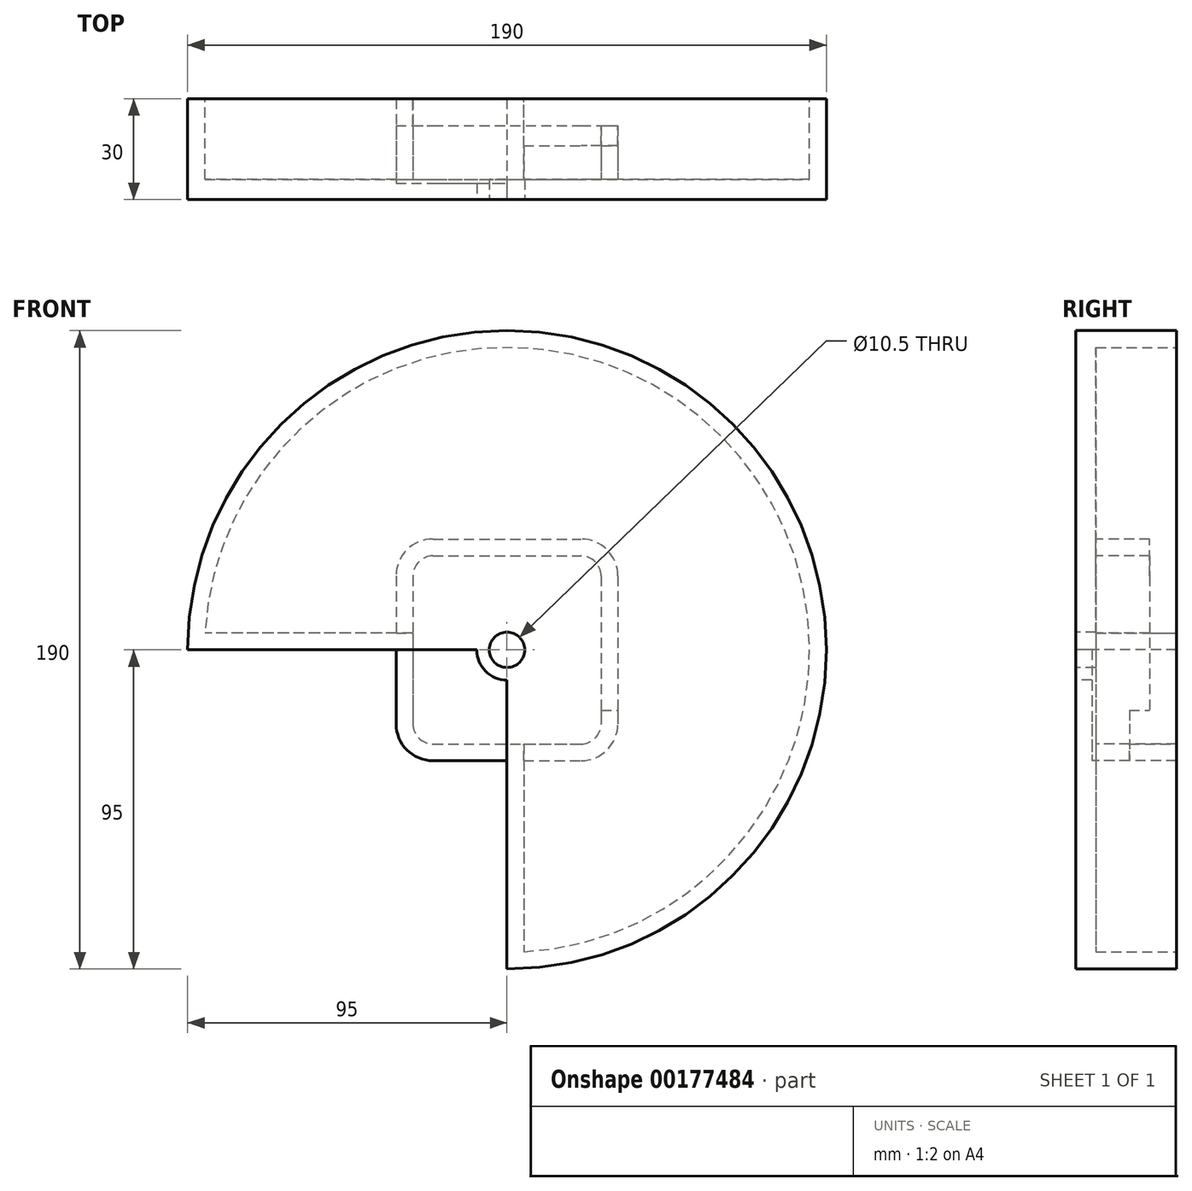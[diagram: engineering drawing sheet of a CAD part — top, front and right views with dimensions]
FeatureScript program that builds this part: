
annotation { "Feature Type Name" : "Feature", "Feature Type Description" : "" }
export const myFeature = defineFeature(function(context is Context, id is Id, definition is map)
    precondition{}
    {
        {
            var Q0;
            Q0=qCreatedBy(makeId("Front.planeOp"),FACE);
            var sketch = newSketch(context, id + "F0", { "sketchPlane" : qUnion([Q0])});
            skCircle(sketch, "E0", {"center": v(0, 0) * mm, "radius": 95 * mm});
            skSolve(sketch);
        }
        {
            var Q0;
            Q0 = qSketchRegion(id + "F0", true);
            extrude(context, id + "F1", {"entities" : qUnion([Q0]), "depth" : 30 * mm});
        }
        {
            var Q0;
            Q0=makeQuery(id+"F1.opExtrude","CAP_FACE",FACE,{"disambiguationData":[OSD([sQuery(id+"F0.wireOp",EDGE,"E0")])],"isStart":false});
            var sketch = newSketch(context, id + "F2", { "sketchPlane" : qUnion([Q0])});
            skLineSegment(sketch, "E1.bottom", {"start": v(-95, 0) * mm, "end": v(0, 0) * mm});
            skLineSegment(sketch, "E1.top", {"start": v(-95, -95) * mm, "end": v(0, -95) * mm});
            skLineSegment(sketch, "E1.left", {"start": v(-95, 0) * mm, "end": v(-95, -95) * mm});
            skLineSegment(sketch, "E1.right", {"start": v(0, 0) * mm, "end": v(0, -95) * mm});
            skSolve(sketch);
        }
        {
            var Q0;
            Q0 = qSketchRegion(id + "F2", true);
            extrude(context, id + "F3", {"entities" : qUnion([Q0]), "operationType" : NewBodyOperationType.REMOVE, "oppositeDirection" : true, "depth" : 40 * mm});
        }
        {
            var Q0;
            Q0=makeQuery(id+"F1.opExtrude","CAP_FACE",FACE,{"disambiguationData":[OSD([sQuery(id+"F0.wireOp",EDGE,"E0")])],"isStart":false});
            var sketch = newSketch(context, id + "F4", { "sketchPlane" : qUnion([Q0])});
            skCircle(sketch, "E2", {"center": v(0, 0) * mm, "radius": 9 * mm});
            skSolve(sketch);
        }
        {
            var Q0;
            Q0 = qSketchRegion(id + "F4", true);
            extrude(context, id + "F5", {"entities" : qUnion([Q0]), "operationType" : NewBodyOperationType.ADD, "oppositeDirection" : true, "depth" : 30 * mm});
        }
        {
            var Q0;
            Q0=makeQuery(id+"F5.boolean.opBoolean","MERGE",FACE,{"derivedFrom":[makeQuery(id+"F1.opExtrude","CAP_FACE",FACE,{"disambiguationData":[OSD([sQuery(id+"F0.wireOp",EDGE,"E0")])],"isStart":false}),makeQuery(id+"F5.opExtrude","CAP_FACE",FACE,{"disambiguationData":[OSD([sQuery(id+"F4.wireOp",EDGE,"E2")])],"isStart":true})]});
            var sketch = newSketch(context, id + "F6", { "sketchPlane" : qUnion([Q0])});
            skCircle(sketch, "E3", {"center": v(0, 0) * mm, "radius": 5.25 * mm});
            skSolve(sketch);
        }
        {
            var Q0;
            Q0 = qSketchRegion(id + "F6", true);
            extrude(context, id + "F7", {"entities" : qUnion([Q0]), "operationType" : NewBodyOperationType.REMOVE, "oppositeDirection" : true, "depth" : 40 * mm});
        }
        {
            var Q0;
            Q0=makeQuery(id+"F5.boolean.opBoolean","MERGE",FACE,{"derivedFrom":[makeQuery(id+"F1.opExtrude","CAP_FACE",FACE,{"disambiguationData":[OSD([sQuery(id+"F0.wireOp",EDGE,"E0")])],"isStart":true}),makeQuery(id+"F5.opExtrude","CAP_FACE",FACE,{"disambiguationData":[OSD([sQuery(id+"F4.wireOp",EDGE,"E2")])],"isStart":false})]});
            var sketch = newSketch(context, id + "F8", { "sketchPlane" : qUnion([Q0])});
            skCircle(sketch, "E4", {"center": v(0, 0) * mm, "radius": 90 * mm});
            skLineSegment(sketch, "E5.bottom", {"start": v(0, -95) * mm, "end": v(95, -95) * mm});
            skLineSegment(sketch, "E5.top", {"start": v(0, 0) * mm, "end": v(95, 0) * mm});
            skLineSegment(sketch, "E5.left", {"start": v(0, -95) * mm, "end": v(0, 0) * mm});
            skLineSegment(sketch, "E5.right", {"start": v(95, -95) * mm, "end": v(95, 0) * mm});
            skLineSegment(sketch, "E6.0", {"start": v(-5, 5) * mm, "end": v(95, 5) * mm});
            skLineSegment(sketch, "E6.1", {"start": v(-5, -95) * mm, "end": v(-5, 5) * mm});
            skSolve(sketch);
        }
        {
            var Q0;
            {var subQ5=makeQuery(id+"F5.opExtrude","CAP_EDGE",EDGE,{"disambiguationData":[OSD([sQuery(id+"F4.wireOp",EDGE,"E2")])],"isStart":false});Q0=makeQuery(id+"F8.imprint","IMPRINT",FACE,{"disambiguationData":[TD([[makeQuery(id+"F8.imprint","IMPRINT",EDGE,{"derivedFrom":subQ5}),1.0]])]});}
            var Q1;
            {var subQ0=sQuery(id+"F8.wireOp",EDGE,"E5.left");var subQ1=sQuery(id+"F8.wireOp",EDGE,"E5.top");var subQ2=makeQuery(id+"F8.imprint","INTERSECT",VERTEX,{"derivedFrom":[subQ1,subQ0]});Q1=makeQuery(id+"F8.imprint","IMPRINT",FACE,{"disambiguationData":[TD([[makeQuery(id+"F8.imprint","IMPRINT",EDGE,{"disambiguationData":[TD([[subQ2,-1.0]])],"derivedFrom":subQ1}),-1.0]])]});}
            var Q2;
            {var subQ0=sQuery(id+"F8.wireOp",EDGE,"E6.1");var subQ1=sQuery(id+"F8.wireOp",EDGE,"E6.0");var subQ2=makeQuery(id+"F8.imprint","INTERSECT",VERTEX,{"derivedFrom":[subQ1,subQ0]});Q2=makeQuery(id+"F8.imprint","IMPRINT",FACE,{"disambiguationData":[TD([[makeQuery(id+"F8.imprint","IMPRINT",EDGE,{"disambiguationData":[TD([[subQ2,-1.0]])],"derivedFrom":subQ1}),-1.0]])]});}
            var Q3;
            {var subQ0=sQuery(id+"F8.wireOp",EDGE,"E6.0");var subQ1=makeQuery(id+"F7.boolean.opBoolean","INTERSECT",EDGE,{"derivedFrom":[makeQuery(id+"F5.boolean.opBoolean","MERGE",FACE,{"derivedFrom":[makeQuery(id+"F1.opExtrude","CAP_FACE",FACE,{"disambiguationData":[OSD([sQuery(id+"F0.wireOp",EDGE,"E0")])],"isStart":true}),makeQuery(id+"F5.opExtrude","CAP_FACE",FACE,{"disambiguationData":[OSD([sQuery(id+"F4.wireOp",EDGE,"E2")])],"isStart":false})]}),makeQuery(id+"F7.opExtrude","SWEPT_FACE",FACE,{"disambiguationData":[OSD([sQuery(id+"F6.wireOp",EDGE,"E3")])]})]});var subQ2=makeQuery(id+"F8.imprint","INTERSECT",VERTEX,{"disambiguationData":[OD(0.0)],"derivedFrom":[subQ1,subQ0]});Q3=makeQuery(id+"F8.imprint","IMPRINT",FACE,{"disambiguationData":[TD([[makeQuery(id+"F8.imprint","IMPRINT",EDGE,{"disambiguationData":[TD([[subQ2,-1.0]])],"derivedFrom":subQ0}),1.0]])]});}
            var Q4;
            {var subQ0=sQuery(id+"F8.wireOp",EDGE,"E6.1");var subQ1=makeQuery(id+"F7.boolean.opBoolean","INTERSECT",EDGE,{"derivedFrom":[makeQuery(id+"F5.boolean.opBoolean","MERGE",FACE,{"derivedFrom":[makeQuery(id+"F1.opExtrude","CAP_FACE",FACE,{"disambiguationData":[OSD([sQuery(id+"F0.wireOp",EDGE,"E0")])],"isStart":true}),makeQuery(id+"F5.opExtrude","CAP_FACE",FACE,{"disambiguationData":[OSD([sQuery(id+"F4.wireOp",EDGE,"E2")])],"isStart":false})]}),makeQuery(id+"F7.opExtrude","SWEPT_FACE",FACE,{"disambiguationData":[OSD([sQuery(id+"F6.wireOp",EDGE,"E3")])]})]});var subQ2=makeQuery(id+"F8.imprint","INTERSECT",VERTEX,{"disambiguationData":[OD(0.0)],"derivedFrom":[subQ1,subQ0]});Q4=makeQuery(id+"F8.imprint","IMPRINT",FACE,{"disambiguationData":[TD([[makeQuery(id+"F8.imprint","IMPRINT",EDGE,{"disambiguationData":[TD([[subQ2,-1.0]])],"derivedFrom":subQ0}),1.0]])]});}
            var Q5;
            {var subQ1=sQuery(id+"F4.wireOp",EDGE,"E2");var subQ2=makeQuery(id+"F5.opExtrude","CAP_EDGE",EDGE,{"disambiguationData":[OSD([subQ1])],"isStart":false});Q5=makeQuery(id+"F8.imprint","IMPRINT",FACE,{"disambiguationData":[TD([[makeQuery(id+"F8.imprint","IMPRINT",EDGE,{"derivedFrom":subQ2}),-1.0]])]});}
            var Q6;
            {var subQ0=sQuery(id+"F8.wireOp",EDGE,"E6.0");var subQ1=sQuery(id+"F8.wireOp",EDGE,"E4");var subQ2=makeQuery(id+"F8.imprint","INTERSECT",VERTEX,{"derivedFrom":[subQ1,subQ0]});Q6=makeQuery(id+"F8.imprint","IMPRINT",FACE,{"disambiguationData":[TD([[makeQuery(id+"F8.imprint","IMPRINT",EDGE,{"disambiguationData":[TD([[subQ2,1.0]])],"derivedFrom":subQ1}),1.0]])]});}
            var Q7;
            {var subQ0=sQuery(id+"F8.wireOp",EDGE,"E6.1");var subQ1=sQuery(id+"F8.wireOp",EDGE,"E4");var subQ2=makeQuery(id+"F8.imprint","INTERSECT",VERTEX,{"derivedFrom":[subQ1,subQ0]});Q7=makeQuery(id+"F8.imprint","IMPRINT",FACE,{"disambiguationData":[TD([[makeQuery(id+"F8.imprint","IMPRINT",EDGE,{"disambiguationData":[TD([[subQ2,-1.0]])],"derivedFrom":subQ1}),1.0]])]});}
            var Q8;
            {var subQ7=sQuery(id+"F8.wireOp",EDGE,"E5.left");var subQ8=sQuery(id+"F8.wireOp",EDGE,"E5.top");var subQ9=makeQuery(id+"F8.imprint","INTERSECT",VERTEX,{"derivedFrom":[subQ8,subQ7]});Q8=makeQuery(id+"F8.imprint","IMPRINT",FACE,{"disambiguationData":[TD([[makeQuery(id+"F8.imprint","IMPRINT",EDGE,{"disambiguationData":[TD([[subQ9,-1.0]])],"derivedFrom":subQ8}),1.0]])]});}
            var Q9;
            {var subQ1=sQuery(id+"F8.wireOp",EDGE,"E4");var subQ5=sQuery(id+"F8.wireOp",EDGE,"E6.0");var subQ6=makeQuery(id+"F8.imprint","INTERSECT",VERTEX,{"derivedFrom":[subQ1,subQ5]});Q9=makeQuery(id+"F8.imprint","IMPRINT",FACE,{"disambiguationData":[TD([[makeQuery(id+"F8.imprint","IMPRINT",EDGE,{"disambiguationData":[TD([[subQ6,-1.0]])],"derivedFrom":subQ1}),1.0]])]});}
            extrude(context, id + "F9", {"entities" : qUnion([Q0, Q1, Q2, Q3, Q4, Q5, Q6, Q7, Q8, Q9]), "operationType" : NewBodyOperationType.REMOVE, "oppositeDirection" : true, "depth" : 24 * mm});
        }
        {
            var Q0;
            Q0=makeQuery(id+"F9.boolean.opBoolean","COPY",FACE,{"derivedFrom":makeQuery(id+"F9.opExtrude","CAP_FACE",FACE,{"disambiguationData":[OSD([sQuery(id+"F8.wireOp",EDGE,"E4")])],"isStart":false})});
            var sketch = newSketch(context, id + "F10", { "sketchPlane" : qUnion([Q0])});
            skLineSegment(sketch, "E7.bottom", {"start": v(28, 28) * mm, "end": v(-28, 28) * mm});
            skLineSegment(sketch, "E7.top", {"start": v(28, -28) * mm, "end": v(-28, -28) * mm});
            skLineSegment(sketch, "E7.left", {"start": v(28, 28) * mm, "end": v(28, -28) * mm});
            skLineSegment(sketch, "E7.right", {"start": v(-28, 28) * mm, "end": v(-28, -28) * mm});
            skPoint(sketch, "E7.middle", {"position": v(0, 0) * mm});
            skLineSegment(sketch, "E8.0", {"start": v(33, 33) * mm, "end": v(-33, 33) * mm});
            skLineSegment(sketch, "E8.1", {"start": v(33, 33) * mm, "end": v(33, -33) * mm});
            skLineSegment(sketch, "E8.2", {"start": v(33, -33) * mm, "end": v(-33, -33) * mm});
            skLineSegment(sketch, "E8.3", {"start": v(-33, 33) * mm, "end": v(-33, -33) * mm});
            skLineSegment(sketch, "E9.bottom", {"start": v(33, 0) * mm, "end": v(90, 0) * mm});
            skLineSegment(sketch, "E9.top", {"start": v(33, 5) * mm, "end": v(90, 5) * mm});
            skLineSegment(sketch, "E9.left", {"start": v(33, 0) * mm, "end": v(33, 5) * mm});
            skLineSegment(sketch, "E9.right", {"start": v(90, 0) * mm, "end": v(90, 5) * mm});
            skLineSegment(sketch, "E10.bottom", {"start": v(0, -33) * mm, "end": v(-5, -33) * mm});
            skLineSegment(sketch, "E10.top", {"start": v(0, -90) * mm, "end": v(-5, -90) * mm});
            skLineSegment(sketch, "E10.left", {"start": v(0, -33) * mm, "end": v(0, -90) * mm});
            skLineSegment(sketch, "E10.right", {"start": v(-5, -33) * mm, "end": v(-5, -90) * mm});
            skSolve(sketch);
        }
        {
            var Q0;
            Q0 = qSketchRegion(id + "F10", true);
            extrude(context, id + "F11", {"entities" : qUnion([Q0]), "operationType" : NewBodyOperationType.ADD, "depth" : 24 * mm});
        }
        {
            var Q0;
            Q0=makeQuery(id+"F11.opExtrude","CAP_FACE",FACE,{"disambiguationData":[OSD([sQuery(id+"F10.wireOp",EDGE,"E7.bottom"),sQuery(id+"F10.wireOp",EDGE,"E7.top"),sQuery(id+"F10.wireOp",EDGE,"E7.left"),sQuery(id+"F10.wireOp",EDGE,"E7.right"),sQuery(id+"F10.wireOp",EDGE,"E8.0"),sQuery(id+"F10.wireOp",EDGE,"E8.1"),sQuery(id+"F10.wireOp",EDGE,"E8.2"),sQuery(id+"F10.wireOp",EDGE,"E8.3"),sQuery(id+"F10.wireOp",EDGE,"E9.bottom"),sQuery(id+"F10.wireOp",EDGE,"E9.top"),sQuery(id+"F10.wireOp",EDGE,"E9.right"),sQuery(id+"F10.wireOp",EDGE,"E10.top"),sQuery(id+"F10.wireOp",EDGE,"E10.left"),sQuery(id+"F10.wireOp",EDGE,"E10.right")])],"isStart":true});
            var sketch = newSketch(context, id + "F12", { "sketchPlane" : qUnion([Q0])});
            skLineSegment(sketch, "E11.0", {"start": v(-28, -28) * mm, "end": v(0, -28) * mm});
            skLineSegment(sketch, "E12.0", {"start": v(-28, 0) * mm, "end": v(-28, -28) * mm});
            skLineSegment(sketch, "E13.0", {"start": v(0, -9) * mm, "end": v(0, -28) * mm});
            skArc(sketch, "E14.0", {"start": v(-9, 0) * mm, "mid": v(-6.36, -6.36) * mm, "end": v(0, -9) * mm});
            skLineSegment(sketch, "E15.0", {"start": v(-28, 0) * mm, "end": v(-9, 0) * mm});
            skLineSegment(sketch, "E16.0", {"start": v(0, -28) * mm, "end": v(0, -33) * mm});
            skLineSegment(sketch, "E17.0", {"start": v(-33, -33) * mm, "end": v(0, -33) * mm});
            skLineSegment(sketch, "E18.0", {"start": v(-33, 0) * mm, "end": v(-33, -33) * mm});
            skLineSegment(sketch, "E19.0", {"start": v(-33, 0) * mm, "end": v(-28, 0) * mm});
            skSolve(sketch);
        }
        {
            var Q0;
            Q0 = qSketchRegion(id + "F12", true);
            extrude(context, id + "F13", {"entities" : qUnion([Q0]), "operationType" : NewBodyOperationType.ADD, "depth" : 1.2 * mm});
        }
        {
            var Q0;
            Q0=makeQuery(id+"F11.boolean.opBoolean","MERGE",FACE,{"derivedFrom":[makeQuery(id+"F5.boolean.opBoolean","MERGE",FACE,{"derivedFrom":[makeQuery(id+"F1.opExtrude","CAP_FACE",FACE,{"disambiguationData":[OSD([sQuery(id+"F0.wireOp",EDGE,"E0")])],"isStart":true}),makeQuery(id+"F5.opExtrude","CAP_FACE",FACE,{"disambiguationData":[OSD([sQuery(id+"F4.wireOp",EDGE,"E2")])],"isStart":false})]}),makeQuery(id+"F11.opExtrude","CAP_FACE",FACE,{"disambiguationData":[OSD([sQuery(id+"F10.wireOp",EDGE,"E7.bottom"),sQuery(id+"F10.wireOp",EDGE,"E7.top"),sQuery(id+"F10.wireOp",EDGE,"E7.left"),sQuery(id+"F10.wireOp",EDGE,"E7.right"),sQuery(id+"F10.wireOp",EDGE,"E8.0"),sQuery(id+"F10.wireOp",EDGE,"E8.1"),sQuery(id+"F10.wireOp",EDGE,"E8.2"),sQuery(id+"F10.wireOp",EDGE,"E8.3"),sQuery(id+"F10.wireOp",EDGE,"E9.bottom"),sQuery(id+"F10.wireOp",EDGE,"E9.top"),sQuery(id+"F10.wireOp",EDGE,"E9.right"),sQuery(id+"F10.wireOp",EDGE,"E10.top"),sQuery(id+"F10.wireOp",EDGE,"E10.left"),sQuery(id+"F10.wireOp",EDGE,"E10.right")])],"isStart":false})]});
            var sketch = newSketch(context, id + "F14", { "sketchPlane" : qUnion([Q0])});
            skLineSegment(sketch, "E20.bottom", {"start": v(-33, 33) * mm, "end": v(33, 33) * mm});
            skLineSegment(sketch, "E20.top", {"start": v(-33, -33) * mm, "end": v(33, -33) * mm});
            skLineSegment(sketch, "E20.left", {"start": v(-33, 33) * mm, "end": v(-33, -33) * mm});
            skLineSegment(sketch, "E20.right", {"start": v(33, 33) * mm, "end": v(33, -33) * mm});
            skLineSegment(sketch, "E21.bottom", {"start": v(33, 5) * mm, "end": v(28, 5) * mm});
            skLineSegment(sketch, "E21.top", {"start": v(33, -28) * mm, "end": v(28, -28) * mm});
            skLineSegment(sketch, "E21.left", {"start": v(33, 5) * mm, "end": v(33, -28) * mm});
            skLineSegment(sketch, "E21.right", {"start": v(28, 5) * mm, "end": v(28, -28) * mm});
            skLineSegment(sketch, "E22.bottom", {"start": v(-5, -33) * mm, "end": v(33, -33) * mm});
            skLineSegment(sketch, "E22.top", {"start": v(-5, -28) * mm, "end": v(33, -28) * mm});
            skLineSegment(sketch, "E22.left", {"start": v(-5, -33) * mm, "end": v(-5, -28) * mm});
            skLineSegment(sketch, "E22.right", {"start": v(33, -33) * mm, "end": v(33, -28) * mm});
            skSolve(sketch);
        }
        {
            var Q0;
            Q0=makeQuery(id+"F14.imprint","IMPRINT",FACE,{"disambiguationData":[TD([[makeQuery(id+"F14.imprint","IMPRINT",EDGE,{"derivedFrom":sQuery(id+"F14.wireOp",EDGE,"E20.bottom")}),1.0]])]});
            extrude(context, id + "F15", {"entities" : qUnion([Q0]), "operationType" : NewBodyOperationType.REMOVE, "oppositeDirection" : true, "depth" : 8 * mm});
        }
        {
            var Q0;
            Q0=makeQuery(id+"F11.opExtrude","SWEPT_EDGE",EDGE,{"disambiguationData":[OSD([sQuery(id+"F10.wireOp",EDGE,"E7.top"),sQuery(id+"F10.wireOp",EDGE,"E7.left")])]});
            var Q1;
            Q1=makeQuery(id+"F11.opExtrude","SWEPT_EDGE",EDGE,{"disambiguationData":[OSD([sQuery(id+"F10.wireOp",EDGE,"E7.top"),sQuery(id+"F10.wireOp",EDGE,"E7.right")])]});
            var Q2;
            Q2=makeQuery(id+"F11.opExtrude","SWEPT_EDGE",EDGE,{"disambiguationData":[OSD([sQuery(id+"F10.wireOp",EDGE,"E7.bottom"),sQuery(id+"F10.wireOp",EDGE,"E7.right")])]});
            var Q3;
            Q3=makeQuery(id+"F11.opExtrude","SWEPT_EDGE",EDGE,{"disambiguationData":[OSD([sQuery(id+"F10.wireOp",EDGE,"E7.bottom"),sQuery(id+"F10.wireOp",EDGE,"E7.left")])]});
            fillet(context, id + "F16", {"entities" : qUnion([Q0, Q1, Q2, Q3]), "radius" : 6 * mm, "tangentPropagation" : true, "allowEdgeOverflow" : false});
        }
        {
            var Q0;
            Q0=makeQuery(id+"F15.boolean.opBoolean","COPY",FACE,{"derivedFrom":makeQuery(id+"F15.opExtrude","CAP_FACE",FACE,{"disambiguationData":[OSD([sQuery(id+"F10.wireOp",EDGE,"E7.bottom"),sQuery(id+"F10.wireOp",EDGE,"E7.top"),sQuery(id+"F10.wireOp",EDGE,"E7.left"),sQuery(id+"F10.wireOp",EDGE,"E7.right"),sQuery(id+"F14.wireOp",EDGE,"E20.bottom"),sQuery(id+"F14.wireOp",EDGE,"E20.top"),sQuery(id+"F14.wireOp",EDGE,"E20.left"),sQuery(id+"F14.wireOp",EDGE,"E20.right"),sQuery(id+"F14.wireOp",EDGE,"E21.bottom"),sQuery(id+"F14.wireOp",EDGE,"E22.left")])],"isStart":false})});
            var sketch = newSketch(context, id + "F17", { "sketchPlane" : qUnion([Q0])});
            skLineSegment(sketch, "E23.bottom", {"start": v(-5, -33) * mm, "end": v(-33, -33) * mm});
            skLineSegment(sketch, "E23.top", {"start": v(-5, -18) * mm, "end": v(-33, -18) * mm});
            skLineSegment(sketch, "E23.left", {"start": v(-5, -33) * mm, "end": v(-5, -18) * mm});
            skLineSegment(sketch, "E23.right", {"start": v(-33, -33) * mm, "end": v(-33, -18) * mm});
            skSolve(sketch);
        }
        {
            var Q0;
            Q0 = qSketchRegion(id + "F17", true);
            extrude(context, id + "F18", {"entities" : qUnion([Q0]), "operationType" : NewBodyOperationType.REMOVE, "oppositeDirection" : true, "depth" : 6 * mm});
        }
        {
            var Q0;
            Q0=makeQuery(id+"F11.opExtrude","SWEPT_EDGE",EDGE,{"disambiguationData":[OSD([sQuery(id+"F10.wireOp",EDGE,"E8.2"),sQuery(id+"F10.wireOp",EDGE,"E8.3")])]});
            var Q1;
            Q1=makeQuery(id+"F13.boolean.opBoolean","MERGE",EDGE,{"derivedFrom":[makeQuery(id+"F11.opExtrude","SWEPT_EDGE",EDGE,{"disambiguationData":[OSD([sQuery(id+"F10.wireOp",EDGE,"E8.1"),sQuery(id+"F10.wireOp",EDGE,"E8.2")])]}),makeQuery(id+"F13.opExtrude","SWEPT_EDGE",EDGE,{"disambiguationData":[OSD([sQuery(id+"F12.wireOp",EDGE,"E17.0"),sQuery(id+"F12.wireOp",EDGE,"E18.0")])]})]});
            var Q2;
            Q2=makeQuery(id+"F11.opExtrude","SWEPT_EDGE",EDGE,{"disambiguationData":[OSD([sQuery(id+"F10.wireOp",EDGE,"E8.0"),sQuery(id+"F10.wireOp",EDGE,"E8.3")])]});
            var Q3;
            Q3=makeQuery(id+"F11.opExtrude","SWEPT_EDGE",EDGE,{"disambiguationData":[OSD([sQuery(id+"F10.wireOp",EDGE,"E8.0"),sQuery(id+"F10.wireOp",EDGE,"E8.1")])]});
            fillet(context, id + "F19", {"entities" : qUnion([Q0, Q1, Q2, Q3]), "radius" : 11 * mm, "tangentPropagation" : true, "allowEdgeOverflow" : false});
        }
    });
